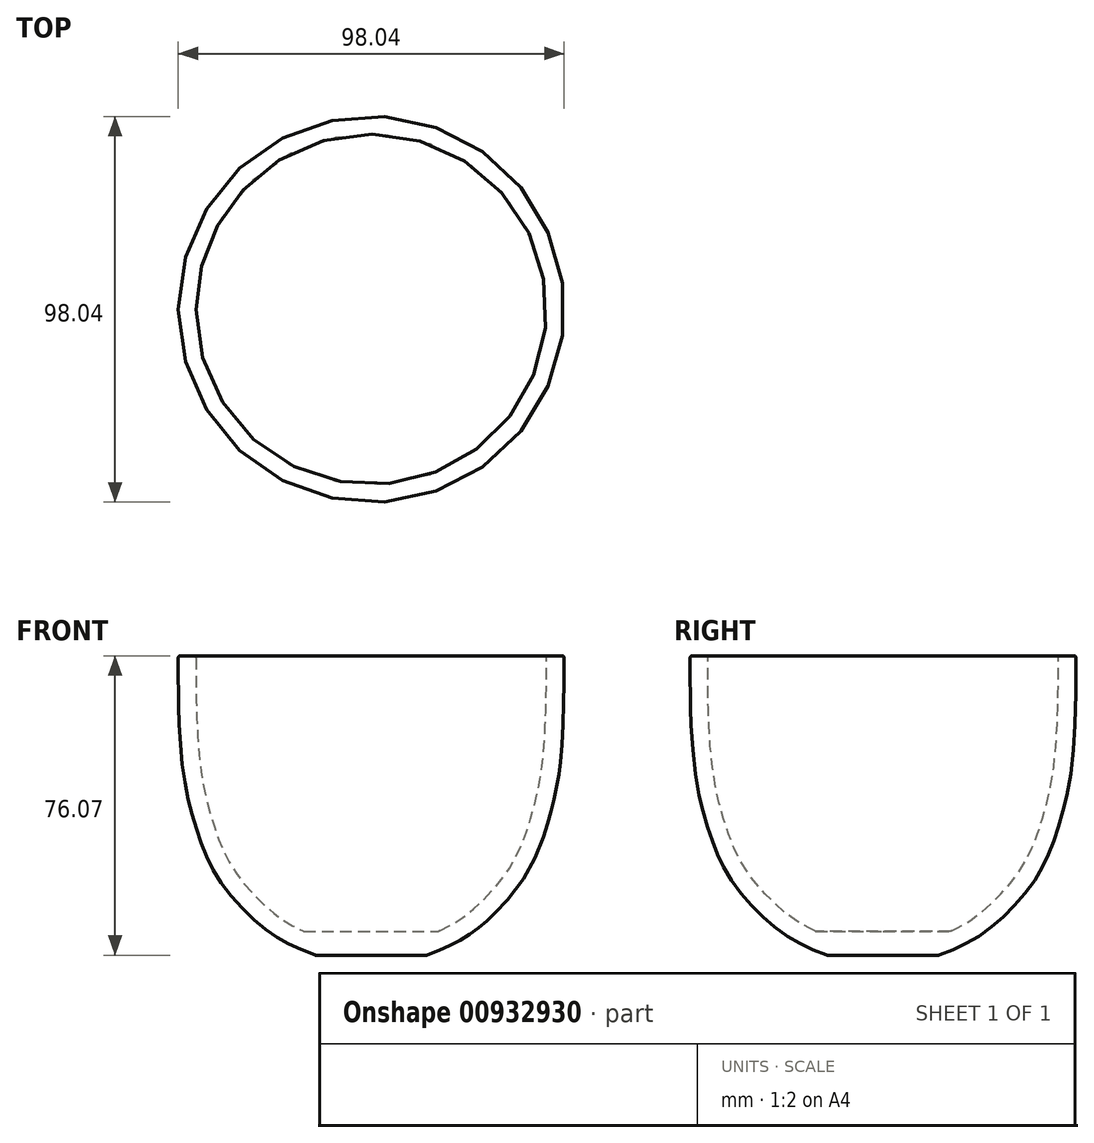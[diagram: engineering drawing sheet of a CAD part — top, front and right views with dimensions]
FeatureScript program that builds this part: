
annotation { "Feature Type Name" : "Feature", "Feature Type Description" : "" }
export const myFeature = defineFeature(function(context is Context, id is Id, definition is map)
    precondition{}
    {
        {
            var Q0;
            Q0=qCreatedBy(makeId("Front.planeOp"),FACE);
            var sketch = newSketch(context, id + "F0", { "sketchPlane" : qUnion([Q0])});
            skLineSegment(sketch, "E0", {"start": v(0, 78.82) * mm, "end": v(-49, 78.82) * mm});
            skLineSegment(sketch, "E1", {"start": v(0, 0) * mm, "end": v(0, 78.82) * mm});
            skFitSpline(sketch, "E2", {"points": [v(-49, 78.82) * mm, v(-49, 71.2) * mm, v(-47.95, 50.94) * mm, v(-44.24, 34.32) * mm, v(-38.54, 21.8) * mm, v(-27.37, 9.77) * mm, v(-17.3, 3.96) * mm, v(0, 0) * mm], "startDerivative": vector(-0.53, -120.05) * mm, "endDerivative": vector(126.32, 0) * mm});
            skSolve(sketch);
        }
        {
            var Q0;
            Q0=qSketchRegion(id+"F0",true);
            var Q1;
            Q1=sQuery(id+"F0.wireOp",EDGE,"E1");
            revolve(context, id + "F1", {"surfaceOperationType" : NewSurfaceOperationType.NEW, "entities" : qUnion([Q0]), "axis" : qUnion([Q1]), "revolveType" : RevolveType.FULL});
        }
        {
            var Q0;
            Q0=makeQuery(id+"F1.opRevolve","SWEPT_FACE",FACE,{"disambiguationData":[OSD([sQuery(id+"F0.wireOp",EDGE,"E0")])]});
            shell(context, id + "F2", {"entities" : qUnion([Q0]), "thickness" : 4.5 * mm});
        }
        {
            var Q0;
            Q0=makeQuery(id+"F1.opRevolve","SWEPT_EDGE",EDGE,{"disambiguationData":[OSD([sQuery(id+"F0.wireOp",EDGE,"E0"),sQuery(id+"F0.wireOp",EDGE,"E2")])]});
            var Q1;
            Q1=makeQuery(id+"F2.opShell","OFFSET_EDGE",EDGE,{"disambiguationData":[OSD([sQuery(id+"F0.wireOp",EDGE,"E0"),sQuery(id+"F0.wireOp",EDGE,"E2")])]});
            fillet(context, id + "F3", {"entities" : qUnion([Q0, Q1]), "radius" : .5 * mm, "tangentPropagation" : true, "defaultsChanged" : true, "vertexSettings" : [], "allowEdgeOverflow" : false});
        }
        {
            var Q0;
            Q0=qCreatedBy(makeId("Front.planeOp"),FACE);
            var sketch = newSketch(context, id + "F4", { "sketchPlane" : qUnion([Q0])});
            skLineSegment(sketch, "E3", {"start": v(-41.77, 30.38) * mm, "end": v(-53.43, 30.38) * mm});
            skLineSegment(sketch, "E4", {"start": v(-49.23, 20.12) * mm, "end": v(-36.53, 20.12) * mm});
            skLineSegment(sketch, "E5", {"start": v(-36.53, 20.12) * mm, "end": v(-41.77, 30.38) * mm});
            skFitSpline(sketch, "E6", {"points": [v(-42.03, 8) * mm, v(-47.44, 16.94) * mm, v(-49.23, 20.12) * mm, v(-51.33, 24.44) * mm, v(-53.43, 30.38) * mm, v(-55.23, 38.72) * mm, v(-56.67, 49.18) * mm, v(-57.32, 61.86) * mm, v(-57.58, 68.13) * mm, v(-57.6, 68.09) * mm], "startDerivative": vector(-47.1, 69.03) * mm, "endDerivative": vector(-6.03, -13.35) * mm});
            skLineSegment(sketch, "E7", {"start": v(-57.58, 68.13) * mm, "end": v(-69.83, 68.13) * mm});
            skFitSpline(sketch, "E8", {"points": [v(-69.83, 68.13) * mm, v(-69.83, 61.07) * mm, v(-69.06, 51.29) * mm, v(-67.63, 40.46) * mm, v(-65.54, 31.18) * mm, v(-63.64, 25) * mm, v(-58.64, 14.66) * mm, v(-54.3, 8) * mm], "startDerivative": vector(-1.12, -53.42) * mm, "endDerivative": vector(31.44, -44.67) * mm});
            skLineSegment(sketch, "E9", {"start": v(-54.3, 8) * mm, "end": v(-42.03, 8) * mm});
            skSolve(sketch);
        }
        {
            var Q0;
            Q0=qCreatedBy(makeId("Right.planeOp"),FACE);
            cPlane(context, id + "F5", {"entities" : qUnion([Q0]), "cplaneType" : CPlaneType.OFFSET, "offset" : 55 * mm, "oppositeDirection" : true, "width" : 150 * mm, "height" : 150 * mm});
        }
        {
            var Q0;
            Q0=qCreatedBy(id+"F5.planeOp",FACE);
            var sketch = newSketch(context, id + "F6", { "sketchPlane" : qUnion([Q0])});
            skPoint(sketch, "E10.middle", {"position": v(0, 24.44) * mm});
            skCircle(sketch, "E11", {"center": v(0, 24.44) * mm, "radius": 6 * mm});
            skSolve(sketch);
        }
        {
            var Q0;
            Q0=qCreatedBy(makeId("Front.planeOp"),FACE);
            var sketch = newSketch(context, id + "F7", { "sketchPlane" : qUnion([Q0])});
            skLineSegment(sketch, "E12", {"start": v(0, 1.35) * mm, "end": v(0, 8.85) * mm});
            skLineSegment(sketch, "E13", {"start": v(0, 8.85) * mm, "end": v(-21, 8.85) * mm});
            skLineSegment(sketch, "E14", {"start": v(-21, 8.85) * mm, "end": v(0, 1.35) * mm});
            skSolve(sketch);
        }
        {
            var Q0;
            Q0=qSketchRegion(id+"F7",true);
            var Q1;
            Q1=sQuery(id+"F7.wireOp",EDGE,"E12");
            revolve(context, id + "F8", {"operationType" : NewBodyOperationType.ADD, "surfaceOperationType" : NewSurfaceOperationType.NEW, "entities" : qUnion([Q0]), "axis" : qUnion([Q1]), "revolveType" : RevolveType.FULL});
        }
        {
            var Q0;
            Q0=qCreatedBy(makeId("Front.planeOp"),FACE);
            var sketch = newSketch(context, id + "F9", { "sketchPlane" : qUnion([Q0])});
            skLineSegment(sketch, "E15.bottom", {"start": v(20, 0) * mm, "end": v(-20, 0) * mm});
            skLineSegment(sketch, "E15.top", {"start": v(20, 2.75) * mm, "end": v(-20, 2.75) * mm});
            skLineSegment(sketch, "E15.left", {"start": v(20, 0) * mm, "end": v(20, 2.75) * mm});
            skLineSegment(sketch, "E15.right", {"start": v(-20, 0) * mm, "end": v(-20, 2.75) * mm});
            skSolve(sketch);
        }
        {
            var Q0;
            Q0=qSketchRegion(id+"F9",true);
            extrude(context, id + "F10", {"entities" : qUnion([Q0]), "operationType" : NewBodyOperationType.REMOVE, "oppositeDirection" : true, "depth" : 40 * mm, "offsetDistance" : 25 * mm, "symmetric" : true});
        }
        {
            var Q0;
            Q0=makeQuery(id+"F10.boolean.opBoolean","INTERSECT",EDGE,{"derivedFrom":[makeQuery(id+"F1.opRevolve","SWEPT_FACE",FACE,{"disambiguationData":[OSD([sQuery(id+"F0.wireOp",EDGE,"E2")])]}),makeQuery(id+"F10.opExtrude","SWEPT_FACE",FACE,{"disambiguationData":[OSD([sQuery(id+"F9.wireOp",EDGE,"E15.top")])]})]});
            var Q1;
            Q1=makeQuery(id+"F8.boolean.opBoolean","INTERSECT",EDGE,{"derivedFrom":[makeQuery(id+"F2.opShell","OFFSET_FACE",FACE,{"disambiguationData":[OSD([sQuery(id+"F0.wireOp",EDGE,"E2")])]}),makeQuery(id+"F8.opRevolve","SWEPT_FACE",FACE,{"disambiguationData":[OSD([sQuery(id+"F7.wireOp",EDGE,"E13")])]})]});
            fillet(context, id + "F11", {"entities" : qUnion([Q0, Q1]), "tangentPropagation" : true, "radius" : .5 * mm, "defaultsChanged" : true, "vertexSettings" : [], "allowEdgeOverflow" : false});
        }
    });
